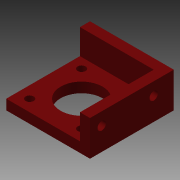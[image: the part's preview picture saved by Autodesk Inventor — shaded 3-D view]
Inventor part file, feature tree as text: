
AUTODESK INVENTOR PART (.ipt)
format: ipt  version: 2014 (Build 180170000, 170)  size: 135,680 bytes
history: native  units: in
note: dims shown in document units (in); Inventor stores cm internally (conversion verified against a paired STEP export)
features: extrude x3, sketch x3
ambient origin geometry x8: Origin, YZ Plane, XZ Plane, XY Plane, X Axis, Y Axis, Z Axis, Center Point
bodies: Solid1 (feature_tree)
feature tree (6):
  extrude  "Extrusion1"  Depth=1.9685in
  extrude  "Extrusion2"  Depth=1.2205in
  extrude  "Extrusion3"  Depth=0.5906in
  sketch  "Sketch1"  dims[d0=1.9685in d1=1.9685in]
  sketch  "Sketch2"  dims[d2=0.187in d3=1.2205in]
  sketch  "Sketch3"  dims[d4=1.2205in d5=0.2756in d6=0.2756in d7=0.9843in d8=0.2362in d9=0.0in d10=0.2362in d11=0.5906in d12=0.0in d13=0.2362in d14=1.2205in d15=0.1969in d16=0.5906in d17=0.0in]
